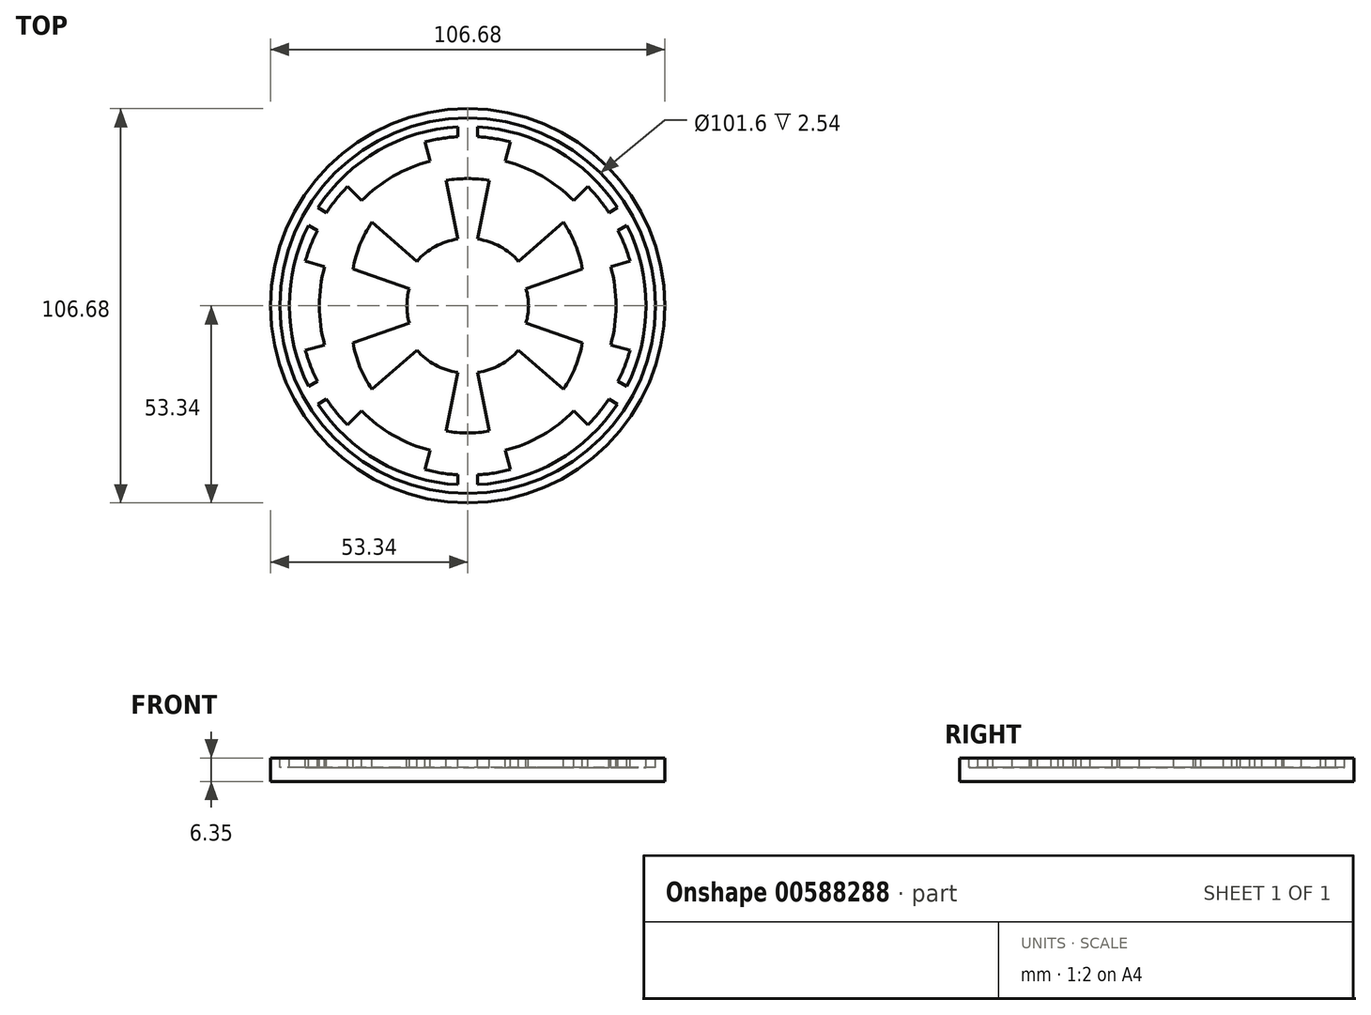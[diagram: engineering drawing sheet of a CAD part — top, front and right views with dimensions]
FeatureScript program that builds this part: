
annotation { "Feature Type Name" : "Feature", "Feature Type Description" : "" }
export const myFeature = defineFeature(function(context is Context, id is Id, definition is map)
    precondition{}
    {
        {
            var Q0;
            Q0=qCreatedBy(makeId("Top.planeOp"),FACE);
            var sketch = newSketch(context, id + "F0", { "sketchPlane" : qUnion([Q0])});
            skCircle(sketch, "E0", {"center": v(0, 0) * mm, "radius": 50.8 * mm});
            skLineSegment(sketch, "E1", {"start": v(0, 0) * mm, "end": v(50.8, 0) * mm});
            skSolve(sketch);
        }
        {
            var Q0;
            Q0=qCreatedBy(makeId("Top.planeOp"),FACE);
            var sketch = newSketch(context, id + "F1", { "sketchPlane" : qUnion([Q0])});
            skArc(sketch, "E2", {"start": v(-48.26, 0) * mm, "mid": v(-46.94, -11.2) * mm, "end": v(-43.06, -21.78) * mm});
            skArc(sketch, "E3", {"start": v(-40.13, 0) * mm, "mid": v(-39.77, -5.35) * mm, "end": v(-38.7, -10.61) * mm});
            skLineSegment(sketch, "E4", {"start": v(-38.7, -10.61) * mm, "end": v(-43.92, -12.04) * mm});
            skArc(sketch, "E5", {"start": v(-43.92, -12.04) * mm, "mid": v(-42.51, -16.3) * mm, "end": v(-40.7, -20.4) * mm});
            skLineSegment(sketch, "E6", {"start": v(-43.06, -21.78) * mm, "end": v(-40.7, -20.4) * mm});
            skArc(sketch, "E7", {"start": v(-40.53, -26.6) * mm, "mid": v(-24.18, -42.02) * mm, "end": v(-2.63, -48.41) * mm});
            skArc(sketch, "E8", {"start": v(-28.67, -28.48) * mm, "mid": v(-20.14, -35.03) * mm, "end": v(-10.18, -39.1) * mm});
            skLineSegment(sketch, "E9", {"start": v(-32.5, -32.26) * mm, "end": v(-28.67, -28.48) * mm});
            skLineSegment(sketch, "E10", {"start": v(-2.63, -48.41) * mm, "end": v(-2.63, -45.74) * mm});
            skLineSegment(sketch, "E11", {"start": v(-10.18, -39.1) * mm, "end": v(-11.56, -44.31) * mm});
            skLineSegment(sketch, "E12", {"start": v(-40.53, -26.6) * mm, "end": v(-38.17, -25.24) * mm});
            skArc(sketch, "E13", {"start": v(-38.17, -25.24) * mm, "mid": v(-35.52, -28.9) * mm, "end": v(-32.5, -32.26) * mm});
            skArc(sketch, "E14", {"start": v(-11.56, -44.31) * mm, "mid": v(-7.13, -45.27) * mm, "end": v(-2.63, -45.74) * mm});
            skLineSegment(sketch, "E15", {"start": v(0, 0) * mm, "end": v(0, -34.4) * mm});
            skArc(sketch, "E16", {"start": v(-5.8, -33.92) * mm, "mid": v(-2.9, -34.28) * mm, "end": v(0, -34.4) * mm});
            skLineSegment(sketch, "E17", {"start": v(-5.8, -33.92) * mm, "end": v(-2.72, -18.06) * mm});
            skArc(sketch, "E18", {"start": v(-13.76, -12) * mm, "mid": v(-8.78, -16.01) * mm, "end": v(-2.72, -18.06) * mm});
            skLineSegment(sketch, "E19", {"start": v(-13.76, -12) * mm, "end": v(-25.92, -22.6) * mm});
            skArc(sketch, "E20", {"start": v(-31.01, -9.96) * mm, "mid": v(-29.15, -16.55) * mm, "end": v(-25.92, -22.6) * mm});
            skLineSegment(sketch, "E21", {"start": v(-31.01, -9.96) * mm, "end": v(-15.78, -4.65) * mm});
            skArc(sketch, "E22", {"start": v(-16.45, 0) * mm, "mid": v(-16.28, -2.35) * mm, "end": v(-15.78, -4.65) * mm});
            skLineSegment(sketch, "E23.MirrorCS", {"start": v(0, 0) * mm, "end": v(0, -34.52) * mm});
            skLineSegment(sketch, "E24.MirrorCS", {"start": v(2.63, -48.41) * mm, "end": v(2.63, -45.74) * mm});
            skLineSegment(sketch, "E25.MirrorCS", {"start": v(5.8, -33.92) * mm, "end": v(2.72, -18.06) * mm});
            skLineSegment(sketch, "E26.MirrorCS", {"start": v(10.18, -39.1) * mm, "end": v(11.56, -44.31) * mm});
            skLineSegment(sketch, "E27.MirrorCS", {"start": v(38.7, -10.61) * mm, "end": v(43.92, -12.04) * mm});
            skLineSegment(sketch, "E28.MirrorCS", {"start": v(43.06, -21.78) * mm, "end": v(40.7, -20.4) * mm});
            skLineSegment(sketch, "E29.MirrorCS", {"start": v(40.53, -26.6) * mm, "end": v(38.17, -25.24) * mm});
            skLineSegment(sketch, "E30.MirrorCS", {"start": v(32.5, -32.26) * mm, "end": v(28.67, -28.48) * mm});
            skArc(sketch, "E31.MirrorCS", {"start": v(11.56, -44.31) * mm, "mid": v(7.13, -45.27) * mm, "end": v(2.63, -45.74) * mm});
            skArc(sketch, "E32.MirrorCS", {"start": v(16.45, 0) * mm, "mid": v(16.28, -2.35) * mm, "end": v(15.78, -4.65) * mm});
            skArc(sketch, "E33.MirrorCS", {"start": v(31.01, -9.96) * mm, "mid": v(29.15, -16.55) * mm, "end": v(25.92, -22.6) * mm});
            skLineSegment(sketch, "E34.MirrorCS", {"start": v(31.01, -9.96) * mm, "end": v(15.78, -4.65) * mm});
            skArc(sketch, "E35.MirrorCS", {"start": v(13.76, -12) * mm, "mid": v(8.78, -16.01) * mm, "end": v(2.72, -18.06) * mm});
            skArc(sketch, "E36.MirrorCS", {"start": v(43.92, -12.04) * mm, "mid": v(42.51, -16.3) * mm, "end": v(40.7, -20.4) * mm});
            skArc(sketch, "E37.MirrorCS", {"start": v(48.26, 0) * mm, "mid": v(46.94, -11.2) * mm, "end": v(43.06, -21.78) * mm});
            skArc(sketch, "E38.MirrorCS", {"start": v(28.67, -28.48) * mm, "mid": v(20.14, -35.03) * mm, "end": v(10.18, -39.1) * mm});
            skLineSegment(sketch, "E39.MirrorCS", {"start": v(13.76, -12) * mm, "end": v(25.92, -22.6) * mm});
            skArc(sketch, "E40.MirrorCS", {"start": v(38.17, -25.24) * mm, "mid": v(35.52, -28.9) * mm, "end": v(32.5, -32.26) * mm});
            skArc(sketch, "E41.MirrorCS", {"start": v(40.13, 0) * mm, "mid": v(39.77, -5.35) * mm, "end": v(38.7, -10.61) * mm});
            skArc(sketch, "E42.MirrorCS", {"start": v(40.53, -26.6) * mm, "mid": v(24.18, -42.02) * mm, "end": v(2.63, -48.41) * mm});
            skArc(sketch, "E43.MirrorCS", {"start": v(5.8, -33.92) * mm, "mid": v(2.9, -34.28) * mm, "end": v(0, -34.4) * mm});
            skLineSegment(sketch, "E44.MirrorCS", {"start": v(2.63, 48.41) * mm, "end": v(2.63, 45.74) * mm});
            skArc(sketch, "E45.MirrorCS", {"start": v(5.8, 33.92) * mm, "mid": v(2.9, 34.28) * mm, "end": v(0, 34.4) * mm});
            skLineSegment(sketch, "E46.MirrorCS", {"start": v(5.8, 33.92) * mm, "end": v(2.72, 18.06) * mm});
            skLineSegment(sketch, "E47.MirrorCS", {"start": v(43.06, 21.78) * mm, "end": v(40.7, 20.4) * mm});
            skLineSegment(sketch, "E48.MirrorCS", {"start": v(40.53, 26.6) * mm, "end": v(38.17, 25.24) * mm});
            skArc(sketch, "E49.MirrorCS", {"start": v(28.67, 28.48) * mm, "mid": v(20.14, 35.03) * mm, "end": v(10.18, 39.1) * mm});
            skArc(sketch, "E50.MirrorCS", {"start": v(40.13, 0) * mm, "mid": v(39.77, 5.35) * mm, "end": v(38.7, 10.61) * mm});
            skArc(sketch, "E51.MirrorCS", {"start": v(31.01, 9.96) * mm, "mid": v(29.15, 16.55) * mm, "end": v(25.92, 22.6) * mm});
            skArc(sketch, "E52.MirrorCS", {"start": v(43.92, 12.04) * mm, "mid": v(42.51, 16.3) * mm, "end": v(40.7, 20.4) * mm});
            skArc(sketch, "E53.MirrorCS", {"start": v(48.26, 0) * mm, "mid": v(46.94, 11.2) * mm, "end": v(43.06, 21.78) * mm});
            skLineSegment(sketch, "E54.MirrorCS", {"start": v(13.76, 12) * mm, "end": v(25.92, 22.6) * mm});
            skArc(sketch, "E55.MirrorCS", {"start": v(38.17, 25.24) * mm, "mid": v(35.52, 28.9) * mm, "end": v(32.5, 32.26) * mm});
            skArc(sketch, "E56.MirrorCS", {"start": v(16.45, 0) * mm, "mid": v(16.28, 2.35) * mm, "end": v(15.78, 4.65) * mm});
            skLineSegment(sketch, "E57.MirrorCS", {"start": v(32.5, 32.26) * mm, "end": v(28.67, 28.48) * mm});
            skLineSegment(sketch, "E58.MirrorCS", {"start": v(10.18, 39.1) * mm, "end": v(11.56, 44.31) * mm});
            skLineSegment(sketch, "E59.MirrorCS", {"start": v(38.7, 10.61) * mm, "end": v(43.92, 12.04) * mm});
            skLineSegment(sketch, "E60.MirrorCS", {"start": v(31.01, 9.96) * mm, "end": v(15.78, 4.65) * mm});
            skArc(sketch, "E61.MirrorCS", {"start": v(40.53, 26.6) * mm, "mid": v(24.18, 42.02) * mm, "end": v(2.63, 48.41) * mm});
            skArc(sketch, "E62.MirrorCS", {"start": v(13.76, 12) * mm, "mid": v(8.78, 16.01) * mm, "end": v(2.72, 18.06) * mm});
            skArc(sketch, "E63.MirrorCS", {"start": v(11.56, 44.31) * mm, "mid": v(7.13, 45.27) * mm, "end": v(2.63, 45.74) * mm});
            skLineSegment(sketch, "E64.MirrorCS", {"start": v(-43.06, 21.78) * mm, "end": v(-40.7, 20.4) * mm});
            skLineSegment(sketch, "E65.MirrorCS", {"start": v(-38.7, 10.61) * mm, "end": v(-43.92, 12.04) * mm});
            skLineSegment(sketch, "E66.MirrorCS", {"start": v(-40.53, 26.6) * mm, "end": v(-38.17, 25.24) * mm});
            skLineSegment(sketch, "E67.MirrorCS", {"start": v(-10.18, 39.1) * mm, "end": v(-11.56, 44.31) * mm});
            skLineSegment(sketch, "E68.MirrorCS", {"start": v(-32.5, 32.26) * mm, "end": v(-28.67, 28.48) * mm});
            skArc(sketch, "E69.MirrorCS", {"start": v(-16.45, 0) * mm, "mid": v(-16.28, 2.35) * mm, "end": v(-15.78, 4.65) * mm});
            skArc(sketch, "E70.MirrorCS", {"start": v(-11.56, 44.31) * mm, "mid": v(-7.13, 45.27) * mm, "end": v(-2.63, 45.74) * mm});
            skLineSegment(sketch, "E71.MirrorCS", {"start": v(-13.76, 12) * mm, "end": v(-25.92, 22.6) * mm});
            skArc(sketch, "E72.MirrorCS", {"start": v(-40.13, 0) * mm, "mid": v(-39.77, 5.35) * mm, "end": v(-38.7, 10.61) * mm});
            skLineSegment(sketch, "E73.MirrorCS", {"start": v(-31.01, 9.96) * mm, "end": v(-15.78, 4.65) * mm});
            skLineSegment(sketch, "E74.MirrorCS", {"start": v(-5.8, 33.92) * mm, "end": v(-2.72, 18.06) * mm});
            skArc(sketch, "E75.MirrorCS", {"start": v(-48.26, 0) * mm, "mid": v(-46.94, 11.2) * mm, "end": v(-43.06, 21.78) * mm});
            skLineSegment(sketch, "E76.MirrorCS", {"start": v(-2.63, 48.41) * mm, "end": v(-2.63, 45.74) * mm});
            skArc(sketch, "E77.MirrorCS", {"start": v(-38.17, 25.24) * mm, "mid": v(-35.52, 28.9) * mm, "end": v(-32.5, 32.26) * mm});
            skArc(sketch, "E78.MirrorCS", {"start": v(-43.92, 12.04) * mm, "mid": v(-42.51, 16.3) * mm, "end": v(-40.7, 20.4) * mm});
            skArc(sketch, "E79.MirrorCS", {"start": v(-40.53, 26.6) * mm, "mid": v(-24.18, 42.02) * mm, "end": v(-2.63, 48.41) * mm});
            skArc(sketch, "E80.MirrorCS", {"start": v(-28.67, 28.48) * mm, "mid": v(-20.14, 35.03) * mm, "end": v(-10.18, 39.1) * mm});
            skArc(sketch, "E81.MirrorCS", {"start": v(-31.01, 9.96) * mm, "mid": v(-29.15, 16.55) * mm, "end": v(-25.92, 22.6) * mm});
            skArc(sketch, "E82.MirrorCS", {"start": v(-13.76, 12) * mm, "mid": v(-8.78, 16.01) * mm, "end": v(-2.72, 18.06) * mm});
            skArc(sketch, "E83.MirrorCS", {"start": v(-5.8, 33.92) * mm, "mid": v(-2.9, 34.28) * mm, "end": v(0, 34.4) * mm});
            skSolve(sketch);
        }
        {
            var Q0;
            Q0=qCreatedBy(makeId("Top.planeOp"),FACE);
            var sketch = newSketch(context, id + "F2", { "sketchPlane" : qUnion([Q0])});
            skCircle(sketch, "E84", {"center": v(0, 0) * mm, "radius": 53.34 * mm});
            skLineSegment(sketch, "E85", {"start": v(0, 0) * mm, "end": v(53.34, 0) * mm});
            skSolve(sketch);
        }
        {
            var Q0;
            Q0 = qSketchRegion(id + "F2", true);
            extrude(context, id + "F3", {"entities" : qUnion([Q0]), "oppositeDirection" : true, "depth" : 6.35 * mm, "offsetDistance" : 25.4 * mm});
        }
        {
            var Q0;
            Q0 = qSketchRegion(id + "F0", true);
            extrude(context, id + "F4", {"entities" : qUnion([Q0]), "operationType" : NewBodyOperationType.REMOVE, "oppositeDirection" : true, "depth" : 2.54 * mm, "offsetDistance" : 25.4 * mm});
        }
        {
            var Q0;
            Q0 = qSketchRegion(id + "F1", true);
            extrude(context, id + "F5", {"entities" : qUnion([Q0]), "operationType" : NewBodyOperationType.ADD, "oppositeDirection" : true, "depth" : 2.54 * mm, "offsetDistance" : 25.4 * mm});
        }
    });
